# Revit family: Single Door - Swing
name_source: partatom
category: Doors
units: mm (PartAtom-declared; Revit-internal decimal feet)

## family parameters
Always vertical = Yes
Cut with Voids When Loaded = No
Host = Wall
OmniClass Number = 23.30.10.00
OmniClass Title = Doors
Room Calculation Point = No
Shared = No

## types (1)
- FL-HM 36x84
    (mat) Hardware = Default
    4 ft = 4' - 0"
    5 ft = 5' - 0"
    Analytic Construction = Metal
    Assembly Code = C1020
    Construction Type = FL
    Define Thermal Properties by = Schematic Type
    Exterior = No
    Frame Outset = 0' - 0 1/2"
    Function = Interior
    Heat Transfer Coefficient (U) = 0.652 BTU/(h·ft²·°F)
    Height = 7' - 0"
    Panel Type = Panel : FL
    Rabbet Depth = 0' - 1 15/16"
    Solar Heat Gain Coefficient = 0
    Thermal Resistance (R) = 1.5338 (h·ft²·°F)/BTU
    Thickness = 0' - 1 3/4"
    Type Comments = FL
    Visual Light Transmittance = 0
    Width = 3' - 0"
    w1 = 0' - 0"

## geometry (parser evidence)
native form markers: Blend x12, Sweep x11
no freeform markers — native parametric forms only
